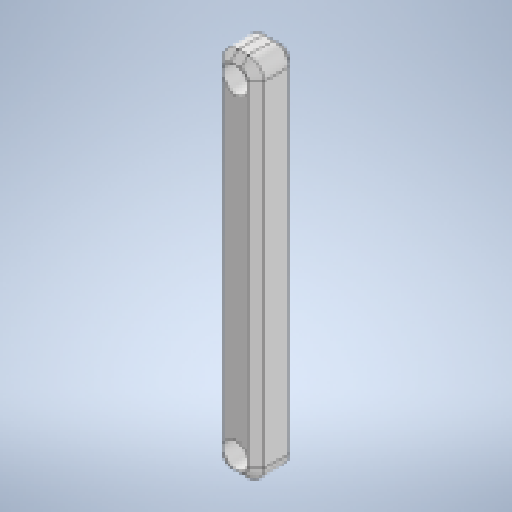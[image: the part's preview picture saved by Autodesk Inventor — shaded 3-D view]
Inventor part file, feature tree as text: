
AUTODESK INVENTOR PART (.ipt)
format: ipt  version: 2024.1 (Build 281209000, 209)  size: 272,384 bytes
history: native  units: mm
features: extrude x1, fillet x1, chamfer x1, sketch x1
ambient origin geometry x8: Origin, YZ Plane, XZ Plane, XY Plane, X Axis, Y Axis, Z Axis, Center Point
bodies: Solid1 (feature_tree)
feature tree (4):
  extrude  "Extrusion1"  Depth=72.0mm
  fillet  "Fillet1"  Radius=5.0mm
  chamfer  "Chamfer1"  Distance=5.0mm
  sketch  "Sketch1"  dims[d0=8.0mm d1=72.0mm d2=5.0mm d3=5.0mm d4=4.0mm d5=64.0mm d7=4.0mm d8=4.0mm d9=8.0mm d10=0.0mm d11=3.0mm d12=1.5mm d13=2.0mm d14=45.0deg]
